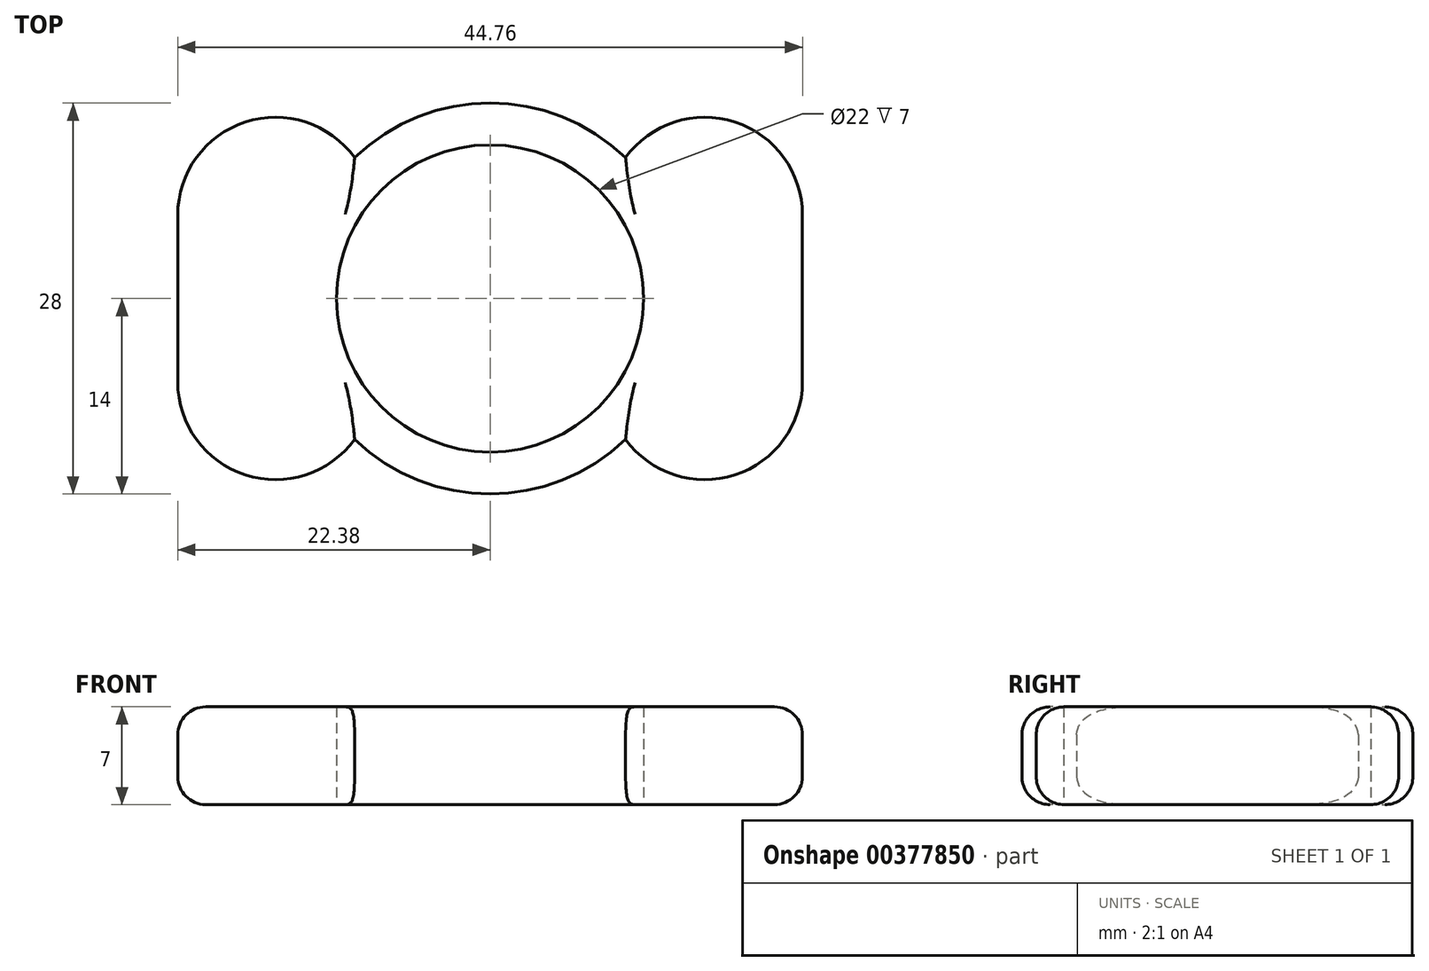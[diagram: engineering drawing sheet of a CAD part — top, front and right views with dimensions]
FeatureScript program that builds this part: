
annotation { "Feature Type Name" : "Feature", "Feature Type Description" : "" }
export const myFeature = defineFeature(function(context is Context, id is Id, definition is map)
    precondition{}
    {
        {
            var Q0;
            Q0=qCreatedBy(makeId("Top.planeOp"),FACE);
            var sketch = newSketch(context, id + "F0", { "sketchPlane" : qUnion([Q0])});
            skCircle(sketch, "E0", {"center": v(0, 0) * mm, "radius": 11 * mm});
            skCircle(sketch, "E1", {"center": v(15.38, -5.98) * mm, "radius": 5.25 * mm});
            skCircle(sketch, "E2", {"center": v(15.38, 5.98) * mm, "radius": 5.25 * mm});
            skCircle(sketch, "E3", {"center": v(-15.38, -5.98) * mm, "radius": 5.25 * mm});
            skCircle(sketch, "E4", {"center": v(-15.38, 5.98) * mm, "radius": 5.25 * mm});
            skCircle(sketch, "E5", {"center": v(0, 0) * mm, "radius": 14 * mm});
            skCircle(sketch, "E6", {"center": v(-15.38, 5.98) * mm, "radius": 7 * mm});
            skCircle(sketch, "E7", {"center": v(-15.38, -5.98) * mm, "radius": 7 * mm});
            skCircle(sketch, "E8", {"center": v(15.38, 5.98) * mm, "radius": 7 * mm});
            skCircle(sketch, "E9", {"center": v(15.38, -5.98) * mm, "radius": 7 * mm});
            skLineSegment(sketch, "E10", {"start": v(-22.38, 5.98) * mm, "end": v(-22.38, -5.98) * mm});
            skLineSegment(sketch, "E11", {"start": v(22.38, 5.98) * mm, "end": v(22.38, -5.98) * mm});
            skLineSegment(sketch, "E12", {"start": v(8.85, -3.44) * mm, "end": v(10.25, -3.99) * mm});
            skLineSegment(sketch, "E13", {"start": v(8.85, 3.44) * mm, "end": v(10.25, 3.99) * mm});
            skLineSegment(sketch, "E14", {"start": v(-8.85, -3.44) * mm, "end": v(-10.25, -3.99) * mm});
            skLineSegment(sketch, "E15", {"start": v(-10.25, -3.99) * mm, "end": v(-8.85, -3.44) * mm});
            skLineSegment(sketch, "E16", {"start": v(-8.85, 3.44) * mm, "end": v(-10.25, 3.99) * mm});
            skSolve(sketch);
        }
        {
            var Q0;
            {var subQ5=sQuery(id+"F0.wireOp",EDGE,"E7");var subQ8=sQuery(id+"F0.wireOp",EDGE,"E0");var subQ10=makeQuery(id+"F0.imprint","INTERSECT",VERTEX,{"disambiguationData":[OD(0.0)],"derivedFrom":[subQ8,subQ5]});Q0=makeQuery(id+"F0.imprint","IMPRINT",FACE,{"disambiguationData":[TD([[makeQuery(id+"F0.imprint","IMPRINT",EDGE,{"disambiguationData":[TD([[subQ10,-1.0]])],"derivedFrom":subQ8}),-1.0]])]});}
            var Q1;
            {var subQ0=sQuery(id+"F0.wireOp",EDGE,"E6");var subQ1=sQuery(id+"F0.wireOp",EDGE,"E3");var subQ11=makeQuery(id+"F0.imprint","INTERSECT",VERTEX,{"disambiguationData":[OD(0.0)],"derivedFrom":[subQ1,subQ0]});Q1=makeQuery(id+"F0.imprint","IMPRINT",FACE,{"disambiguationData":[TD([[makeQuery(id+"F0.imprint","IMPRINT",EDGE,{"disambiguationData":[TD([[subQ11,-1.0]])],"derivedFrom":subQ1}),-1.0]])]});}
            var Q2;
            {var subQ2=sQuery(id+"F0.wireOp",EDGE,"E6");var subQ4=sQuery(id+"F0.wireOp",EDGE,"E3");var subQ5=makeQuery(id+"F0.imprint","INTERSECT",VERTEX,{"disambiguationData":[OD(1.0)],"derivedFrom":[subQ4,subQ2]});Q2=makeQuery(id+"F0.imprint","IMPRINT",FACE,{"disambiguationData":[TD([[makeQuery(id+"F0.imprint","IMPRINT",EDGE,{"disambiguationData":[TD([[subQ5,-1.0]])],"derivedFrom":subQ4}),-1.0]])]});}
            var Q3;
            {var subQ0=sQuery(id+"F0.wireOp",EDGE,"E7");var subQ1=sQuery(id+"F0.wireOp",EDGE,"E5");var subQ2=makeQuery(id+"F0.imprint","INTERSECT",VERTEX,{"disambiguationData":[OD(1.0)],"derivedFrom":[subQ1,subQ0]});Q3=makeQuery(id+"F0.imprint","IMPRINT",FACE,{"disambiguationData":[TD([[makeQuery(id+"F0.imprint","IMPRINT",EDGE,{"disambiguationData":[TD([[subQ2,-1.0]])],"derivedFrom":subQ1}),1.0]])]});}
            var Q4;
            {var subQ0=sQuery(id+"F0.wireOp",EDGE,"E6");var subQ1=sQuery(id+"F0.wireOp",EDGE,"E3");var subQ2=makeQuery(id+"F0.imprint","INTERSECT",VERTEX,{"disambiguationData":[OD(0.0)],"derivedFrom":[subQ1,subQ0]});Q4=makeQuery(id+"F0.imprint","IMPRINT",FACE,{"disambiguationData":[TD([[makeQuery(id+"F0.imprint","IMPRINT",EDGE,{"disambiguationData":[TD([[subQ2,1.0]])],"derivedFrom":subQ1}),-1.0]])]});}
            var Q5;
            {var subQ0=sQuery(id+"F0.wireOp",EDGE,"E7");var subQ1=sQuery(id+"F0.wireOp",EDGE,"E4");var subQ2=makeQuery(id+"F0.imprint","INTERSECT",VERTEX,{"disambiguationData":[OD(1.0)],"derivedFrom":[subQ1,subQ0]});Q5=makeQuery(id+"F0.imprint","IMPRINT",FACE,{"disambiguationData":[TD([[makeQuery(id+"F0.imprint","IMPRINT",EDGE,{"disambiguationData":[TD([[subQ2,-1.0]])],"derivedFrom":subQ1}),-1.0]])]});}
            var Q6;
            {var subQ0=sQuery(id+"F0.wireOp",EDGE,"E6");var subQ1=sQuery(id+"F0.wireOp",EDGE,"E0");var subQ2=makeQuery(id+"F0.imprint","INTERSECT",VERTEX,{"disambiguationData":[OD(1.0)],"derivedFrom":[subQ1,subQ0]});Q6=makeQuery(id+"F0.imprint","IMPRINT",FACE,{"disambiguationData":[TD([[makeQuery(id+"F0.imprint","IMPRINT",EDGE,{"disambiguationData":[TD([[subQ2,-1.0]])],"derivedFrom":subQ1}),-1.0]])]});}
            var Q7;
            {var subQ5=sQuery(id+"F0.wireOp",EDGE,"E6");var subQ9=sQuery(id+"F0.wireOp",EDGE,"E0");var subQ10=makeQuery(id+"F0.imprint","INTERSECT",VERTEX,{"disambiguationData":[OD(0.0)],"derivedFrom":[subQ9,subQ5]});Q7=makeQuery(id+"F0.imprint","IMPRINT",FACE,{"disambiguationData":[TD([[makeQuery(id+"F0.imprint","IMPRINT",EDGE,{"disambiguationData":[TD([[subQ10,-1.0]])],"derivedFrom":subQ9}),-1.0]])]});}
            var Q8;
            {var subQ2=sQuery(id+"F0.wireOp",EDGE,"E7");var subQ4=sQuery(id+"F0.wireOp",EDGE,"E4");var subQ5=makeQuery(id+"F0.imprint","INTERSECT",VERTEX,{"disambiguationData":[OD(0.0)],"derivedFrom":[subQ4,subQ2]});Q8=makeQuery(id+"F0.imprint","IMPRINT",FACE,{"disambiguationData":[TD([[makeQuery(id+"F0.imprint","IMPRINT",EDGE,{"disambiguationData":[TD([[subQ5,1.0]])],"derivedFrom":subQ4}),-1.0]])]});}
            var Q9;
            {var subQ0=sQuery(id+"F0.wireOp",EDGE,"E8");var subQ1=sQuery(id+"F0.wireOp",EDGE,"E0");var subQ2=makeQuery(id+"F0.imprint","INTERSECT",VERTEX,{"disambiguationData":[OD(0.0)],"derivedFrom":[subQ1,subQ0]});Q9=makeQuery(id+"F0.imprint","IMPRINT",FACE,{"disambiguationData":[TD([[makeQuery(id+"F0.imprint","IMPRINT",EDGE,{"disambiguationData":[TD([[subQ2,-1.0]])],"derivedFrom":subQ1}),-1.0]])]});}
            var Q10;
            {var subQ0=sQuery(id+"F0.wireOp",EDGE,"E7");var subQ1=sQuery(id+"F0.wireOp",EDGE,"E0");var subQ2=makeQuery(id+"F0.imprint","INTERSECT",VERTEX,{"disambiguationData":[OD(1.0)],"derivedFrom":[subQ1,subQ0]});Q10=makeQuery(id+"F0.imprint","IMPRINT",FACE,{"disambiguationData":[TD([[makeQuery(id+"F0.imprint","IMPRINT",EDGE,{"disambiguationData":[TD([[subQ2,-1.0]])],"derivedFrom":subQ1}),-1.0]])]});}
            var Q11;
            {var subQ6=sQuery(id+"F0.wireOp",EDGE,"E9");var subQ8=sQuery(id+"F0.wireOp",EDGE,"E0");var subQ9=makeQuery(id+"F0.imprint","INTERSECT",VERTEX,{"disambiguationData":[OD(0.0)],"derivedFrom":[subQ8,subQ6]});Q11=makeQuery(id+"F0.imprint","IMPRINT",FACE,{"disambiguationData":[TD([[makeQuery(id+"F0.imprint","IMPRINT",EDGE,{"disambiguationData":[TD([[subQ9,-1.0]])],"derivedFrom":subQ8}),-1.0]])]});}
            var Q12;
            {var subQ0=sQuery(id+"F0.wireOp",EDGE,"E9");var subQ1=sQuery(id+"F0.wireOp",EDGE,"E5");var subQ2=makeQuery(id+"F0.imprint","INTERSECT",VERTEX,{"disambiguationData":[OD(1.0)],"derivedFrom":[subQ1,subQ0]});Q12=makeQuery(id+"F0.imprint","IMPRINT",FACE,{"disambiguationData":[TD([[makeQuery(id+"F0.imprint","IMPRINT",EDGE,{"disambiguationData":[TD([[subQ2,1.0]])],"derivedFrom":subQ1}),1.0]])]});}
            var Q13;
            {var subQ0=sQuery(id+"F0.wireOp",EDGE,"E8");var subQ5=sQuery(id+"F0.wireOp",EDGE,"E0");var subQ6=makeQuery(id+"F0.imprint","INTERSECT",VERTEX,{"disambiguationData":[OD(0.0)],"derivedFrom":[subQ5,subQ0]});Q13=makeQuery(id+"F0.imprint","IMPRINT",FACE,{"disambiguationData":[TD([[makeQuery(id+"F0.imprint","IMPRINT",EDGE,{"disambiguationData":[TD([[subQ6,1.0]])],"derivedFrom":subQ5}),-1.0]])]});}
            var Q14;
            {var subQ2=sQuery(id+"F0.wireOp",EDGE,"E5");var subQ6=sQuery(id+"F0.wireOp",EDGE,"E2");var subQ7=makeQuery(id+"F0.imprint","INTERSECT",VERTEX,{"disambiguationData":[OD(1.0)],"derivedFrom":[subQ6,subQ2]});Q14=makeQuery(id+"F0.imprint","IMPRINT",FACE,{"disambiguationData":[TD([[makeQuery(id+"F0.imprint","IMPRINT",EDGE,{"disambiguationData":[TD([[subQ7,1.0]])],"derivedFrom":subQ6}),-1.0]])]});}
            var Q15;
            {var subQ0=sQuery(id+"F0.wireOp",EDGE,"E11");Q15=makeQuery(id+"F0.imprint","IMPRINT",FACE,{"disambiguationData":[TD([[makeQuery(id+"F0.imprint","IMPRINT",EDGE,{"derivedFrom":subQ0}),-1.0]])]});}
            var Q16;
            {var subQ2=sQuery(id+"F0.wireOp",EDGE,"E8");var subQ4=sQuery(id+"F0.wireOp",EDGE,"E1");var subQ5=makeQuery(id+"F0.imprint","INTERSECT",VERTEX,{"disambiguationData":[OD(1.0)],"derivedFrom":[subQ4,subQ2]});Q16=makeQuery(id+"F0.imprint","IMPRINT",FACE,{"disambiguationData":[TD([[makeQuery(id+"F0.imprint","IMPRINT",EDGE,{"disambiguationData":[TD([[subQ5,1.0]])],"derivedFrom":subQ4}),-1.0]])]});}
            var Q17;
            {var subQ3=sQuery(id+"F0.wireOp",EDGE,"E8");var subQ8=sQuery(id+"F0.wireOp",EDGE,"E1");var subQ9=makeQuery(id+"F0.imprint","INTERSECT",VERTEX,{"disambiguationData":[OD(0.0)],"derivedFrom":[subQ8,subQ3]});Q17=makeQuery(id+"F0.imprint","IMPRINT",FACE,{"disambiguationData":[TD([[makeQuery(id+"F0.imprint","IMPRINT",EDGE,{"disambiguationData":[TD([[subQ9,1.0]])],"derivedFrom":subQ8}),-1.0]])]});}
            var Q18;
            {var subQ0=sQuery(id+"F0.wireOp",EDGE,"E8");var subQ1=sQuery(id+"F0.wireOp",EDGE,"E0");var subQ2=makeQuery(id+"F0.imprint","INTERSECT",VERTEX,{"disambiguationData":[OD(1.0)],"derivedFrom":[subQ1,subQ0]});Q18=makeQuery(id+"F0.imprint","IMPRINT",FACE,{"disambiguationData":[TD([[makeQuery(id+"F0.imprint","IMPRINT",EDGE,{"disambiguationData":[TD([[subQ2,1.0]])],"derivedFrom":subQ1}),-1.0]])]});}
            var Q19;
            {var subQ0=sQuery(id+"F0.wireOp",EDGE,"E8");var subQ1=sQuery(id+"F0.wireOp",EDGE,"E1");var subQ2=makeQuery(id+"F0.imprint","INTERSECT",VERTEX,{"disambiguationData":[OD(0.0)],"derivedFrom":[subQ1,subQ0]});Q19=makeQuery(id+"F0.imprint","IMPRINT",FACE,{"disambiguationData":[TD([[makeQuery(id+"F0.imprint","IMPRINT",EDGE,{"disambiguationData":[TD([[subQ2,-1.0]])],"derivedFrom":subQ1}),-1.0]])]});}
            var Q20;
            {var subQ0=sQuery(id+"F0.wireOp",EDGE,"E5");var subQ1=sQuery(id+"F0.wireOp",EDGE,"E2");var subQ2=makeQuery(id+"F0.imprint","INTERSECT",VERTEX,{"disambiguationData":[OD(0.0)],"derivedFrom":[subQ1,subQ0]});Q20=makeQuery(id+"F0.imprint","IMPRINT",FACE,{"disambiguationData":[TD([[makeQuery(id+"F0.imprint","IMPRINT",EDGE,{"disambiguationData":[TD([[subQ2,-1.0]])],"derivedFrom":subQ1}),-1.0]])]});}
            var Q21;
            {var subQ0=sQuery(id+"F0.wireOp",EDGE,"E10");Q21=makeQuery(id+"F0.imprint","IMPRINT",FACE,{"disambiguationData":[TD([[makeQuery(id+"F0.imprint","IMPRINT",EDGE,{"derivedFrom":subQ0}),1.0]])]});}
            var Q22;
            {var subQ0=sQuery(id+"F0.wireOp",EDGE,"E8");var subQ1=sQuery(id+"F0.wireOp",EDGE,"E0");var subQ2=makeQuery(id+"F0.imprint","INTERSECT",VERTEX,{"disambiguationData":[OD(1.0)],"derivedFrom":[subQ1,subQ0]});Q22=makeQuery(id+"F0.imprint","IMPRINT",FACE,{"disambiguationData":[TD([[makeQuery(id+"F0.imprint","IMPRINT",EDGE,{"disambiguationData":[TD([[subQ2,-1.0]])],"derivedFrom":subQ1}),-1.0]])]});}
            extrude(context, id + "F1", {"entities" : qUnion([Q0, Q1, Q2, Q3, Q4, Q5, Q6, Q7, Q8, Q9, Q10, Q11, Q12, Q13, Q14, Q15, Q16, Q17, Q18, Q19, Q20, Q21, Q22]), "depth" : 7 * mm});
        }
        {
            var Q0;
            {var subQ5=sQuery(id+"F0.wireOp",EDGE,"E7");var subQ8=sQuery(id+"F0.wireOp",EDGE,"E0");var subQ10=makeQuery(id+"F0.imprint","INTERSECT",VERTEX,{"disambiguationData":[OD(0.0)],"derivedFrom":[subQ8,subQ5]});Q0=makeQuery(id+"F0.imprint","IMPRINT",FACE,{"disambiguationData":[TD([[makeQuery(id+"F0.imprint","IMPRINT",EDGE,{"disambiguationData":[TD([[subQ10,-1.0]])],"derivedFrom":subQ8}),-1.0]])]});}
            var Q1;
            {var subQ2=sQuery(id+"F0.wireOp",EDGE,"E6");var subQ4=sQuery(id+"F0.wireOp",EDGE,"E3");var subQ5=makeQuery(id+"F0.imprint","INTERSECT",VERTEX,{"disambiguationData":[OD(1.0)],"derivedFrom":[subQ4,subQ2]});Q1=makeQuery(id+"F0.imprint","IMPRINT",FACE,{"disambiguationData":[TD([[makeQuery(id+"F0.imprint","IMPRINT",EDGE,{"disambiguationData":[TD([[subQ5,-1.0]])],"derivedFrom":subQ4}),-1.0]])]});}
            var Q2;
            {var subQ0=sQuery(id+"F0.wireOp",EDGE,"E6");var subQ1=sQuery(id+"F0.wireOp",EDGE,"E3");var subQ11=makeQuery(id+"F0.imprint","INTERSECT",VERTEX,{"disambiguationData":[OD(0.0)],"derivedFrom":[subQ1,subQ0]});Q2=makeQuery(id+"F0.imprint","IMPRINT",FACE,{"disambiguationData":[TD([[makeQuery(id+"F0.imprint","IMPRINT",EDGE,{"disambiguationData":[TD([[subQ11,-1.0]])],"derivedFrom":subQ1}),-1.0]])]});}
            var Q3;
            {var subQ2=sQuery(id+"F0.wireOp",EDGE,"E7");var subQ4=sQuery(id+"F0.wireOp",EDGE,"E4");var subQ5=makeQuery(id+"F0.imprint","INTERSECT",VERTEX,{"disambiguationData":[OD(0.0)],"derivedFrom":[subQ4,subQ2]});Q3=makeQuery(id+"F0.imprint","IMPRINT",FACE,{"disambiguationData":[TD([[makeQuery(id+"F0.imprint","IMPRINT",EDGE,{"disambiguationData":[TD([[subQ5,1.0]])],"derivedFrom":subQ4}),-1.0]])]});}
            var Q4;
            {var subQ0=sQuery(id+"F0.wireOp",EDGE,"E8");var subQ1=sQuery(id+"F0.wireOp",EDGE,"E0");var subQ2=makeQuery(id+"F0.imprint","INTERSECT",VERTEX,{"disambiguationData":[OD(0.0)],"derivedFrom":[subQ1,subQ0]});Q4=makeQuery(id+"F0.imprint","IMPRINT",FACE,{"disambiguationData":[TD([[makeQuery(id+"F0.imprint","IMPRINT",EDGE,{"disambiguationData":[TD([[subQ2,-1.0]])],"derivedFrom":subQ1}),-1.0]])]});}
            var Q5;
            {var subQ0=sQuery(id+"F0.wireOp",EDGE,"E5");var subQ1=sQuery(id+"F0.wireOp",EDGE,"E4");var subQ2=makeQuery(id+"F0.imprint","INTERSECT",VERTEX,{"disambiguationData":[OD(0.0)],"derivedFrom":[subQ1,subQ0]});Q5=makeQuery(id+"F0.imprint","IMPRINT",FACE,{"disambiguationData":[TD([[makeQuery(id+"F0.imprint","IMPRINT",EDGE,{"disambiguationData":[TD([[subQ2,1.0]])],"derivedFrom":subQ1}),1.0]])]});}
            var Q6;
            {var subQ0=sQuery(id+"F0.wireOp",EDGE,"E7");var subQ1=sQuery(id+"F0.wireOp",EDGE,"E4");var subQ2=makeQuery(id+"F0.imprint","INTERSECT",VERTEX,{"disambiguationData":[OD(0.0)],"derivedFrom":[subQ1,subQ0]});Q6=makeQuery(id+"F0.imprint","IMPRINT",FACE,{"disambiguationData":[TD([[makeQuery(id+"F0.imprint","IMPRINT",EDGE,{"disambiguationData":[TD([[subQ2,1.0]])],"derivedFrom":subQ1}),1.0]])]});}
            var Q7;
            {var subQ5=sQuery(id+"F0.wireOp",EDGE,"E6");var subQ9=sQuery(id+"F0.wireOp",EDGE,"E0");var subQ10=makeQuery(id+"F0.imprint","INTERSECT",VERTEX,{"disambiguationData":[OD(0.0)],"derivedFrom":[subQ9,subQ5]});Q7=makeQuery(id+"F0.imprint","IMPRINT",FACE,{"disambiguationData":[TD([[makeQuery(id+"F0.imprint","IMPRINT",EDGE,{"disambiguationData":[TD([[subQ10,-1.0]])],"derivedFrom":subQ9}),-1.0]])]});}
            var Q8;
            {var subQ0=sQuery(id+"F0.wireOp",EDGE,"E7");var subQ1=sQuery(id+"F0.wireOp",EDGE,"E5");var subQ2=makeQuery(id+"F0.imprint","INTERSECT",VERTEX,{"disambiguationData":[OD(1.0)],"derivedFrom":[subQ1,subQ0]});Q8=makeQuery(id+"F0.imprint","IMPRINT",FACE,{"disambiguationData":[TD([[makeQuery(id+"F0.imprint","IMPRINT",EDGE,{"disambiguationData":[TD([[subQ2,-1.0]])],"derivedFrom":subQ1}),1.0]])]});}
            var Q9;
            {var subQ0=sQuery(id+"F0.wireOp",EDGE,"E5");var subQ1=sQuery(id+"F0.wireOp",EDGE,"E3");var subQ2=makeQuery(id+"F0.imprint","INTERSECT",VERTEX,{"disambiguationData":[OD(0.0)],"derivedFrom":[subQ1,subQ0]});Q9=makeQuery(id+"F0.imprint","IMPRINT",FACE,{"disambiguationData":[TD([[makeQuery(id+"F0.imprint","IMPRINT",EDGE,{"disambiguationData":[TD([[subQ2,1.0]])],"derivedFrom":subQ1}),1.0]])]});}
            var Q10;
            {var subQ0=sQuery(id+"F0.wireOp",EDGE,"E7");var subQ1=sQuery(id+"F0.wireOp",EDGE,"E0");var subQ2=makeQuery(id+"F0.imprint","INTERSECT",VERTEX,{"disambiguationData":[OD(1.0)],"derivedFrom":[subQ1,subQ0]});Q10=makeQuery(id+"F0.imprint","IMPRINT",FACE,{"disambiguationData":[TD([[makeQuery(id+"F0.imprint","IMPRINT",EDGE,{"disambiguationData":[TD([[subQ2,-1.0]])],"derivedFrom":subQ1}),-1.0]])]});}
            var Q11;
            {var subQ6=sQuery(id+"F0.wireOp",EDGE,"E9");var subQ8=sQuery(id+"F0.wireOp",EDGE,"E0");var subQ9=makeQuery(id+"F0.imprint","INTERSECT",VERTEX,{"disambiguationData":[OD(0.0)],"derivedFrom":[subQ8,subQ6]});Q11=makeQuery(id+"F0.imprint","IMPRINT",FACE,{"disambiguationData":[TD([[makeQuery(id+"F0.imprint","IMPRINT",EDGE,{"disambiguationData":[TD([[subQ9,-1.0]])],"derivedFrom":subQ8}),-1.0]])]});}
            var Q12;
            {var subQ0=sQuery(id+"F0.wireOp",EDGE,"E6");var subQ1=sQuery(id+"F0.wireOp",EDGE,"E3");var subQ2=makeQuery(id+"F0.imprint","INTERSECT",VERTEX,{"disambiguationData":[OD(0.0)],"derivedFrom":[subQ1,subQ0]});Q12=makeQuery(id+"F0.imprint","IMPRINT",FACE,{"disambiguationData":[TD([[makeQuery(id+"F0.imprint","IMPRINT",EDGE,{"disambiguationData":[TD([[subQ2,1.0]])],"derivedFrom":subQ1}),1.0]])]});}
            var Q13;
            {var subQ0=sQuery(id+"F0.wireOp",EDGE,"E5");var subQ1=sQuery(id+"F0.wireOp",EDGE,"E1");var subQ2=makeQuery(id+"F0.imprint","INTERSECT",VERTEX,{"disambiguationData":[OD(0.0)],"derivedFrom":[subQ1,subQ0]});Q13=makeQuery(id+"F0.imprint","IMPRINT",FACE,{"disambiguationData":[TD([[makeQuery(id+"F0.imprint","IMPRINT",EDGE,{"disambiguationData":[TD([[subQ2,-1.0]])],"derivedFrom":subQ1}),1.0]])]});}
            var Q14;
            {var subQ0=sQuery(id+"F0.wireOp",EDGE,"E9");var subQ1=sQuery(id+"F0.wireOp",EDGE,"E5");var subQ2=makeQuery(id+"F0.imprint","INTERSECT",VERTEX,{"disambiguationData":[OD(1.0)],"derivedFrom":[subQ1,subQ0]});Q14=makeQuery(id+"F0.imprint","IMPRINT",FACE,{"disambiguationData":[TD([[makeQuery(id+"F0.imprint","IMPRINT",EDGE,{"disambiguationData":[TD([[subQ2,1.0]])],"derivedFrom":subQ1}),1.0]])]});}
            var Q15;
            {var subQ0=sQuery(id+"F0.wireOp",EDGE,"E8");var subQ5=sQuery(id+"F0.wireOp",EDGE,"E0");var subQ6=makeQuery(id+"F0.imprint","INTERSECT",VERTEX,{"disambiguationData":[OD(0.0)],"derivedFrom":[subQ5,subQ0]});Q15=makeQuery(id+"F0.imprint","IMPRINT",FACE,{"disambiguationData":[TD([[makeQuery(id+"F0.imprint","IMPRINT",EDGE,{"disambiguationData":[TD([[subQ6,1.0]])],"derivedFrom":subQ5}),-1.0]])]});}
            var Q16;
            {var subQ0=sQuery(id+"F0.wireOp",EDGE,"E5");var subQ1=sQuery(id+"F0.wireOp",EDGE,"E2");var subQ2=makeQuery(id+"F0.imprint","INTERSECT",VERTEX,{"disambiguationData":[OD(0.0)],"derivedFrom":[subQ1,subQ0]});Q16=makeQuery(id+"F0.imprint","IMPRINT",FACE,{"disambiguationData":[TD([[makeQuery(id+"F0.imprint","IMPRINT",EDGE,{"disambiguationData":[TD([[subQ2,1.0]])],"derivedFrom":subQ1}),1.0]])]});}
            var Q17;
            {var subQ2=sQuery(id+"F0.wireOp",EDGE,"E5");var subQ6=sQuery(id+"F0.wireOp",EDGE,"E2");var subQ7=makeQuery(id+"F0.imprint","INTERSECT",VERTEX,{"disambiguationData":[OD(1.0)],"derivedFrom":[subQ6,subQ2]});Q17=makeQuery(id+"F0.imprint","IMPRINT",FACE,{"disambiguationData":[TD([[makeQuery(id+"F0.imprint","IMPRINT",EDGE,{"disambiguationData":[TD([[subQ7,1.0]])],"derivedFrom":subQ6}),-1.0]])]});}
            var Q18;
            {var subQ3=sQuery(id+"F0.wireOp",EDGE,"E8");var subQ8=sQuery(id+"F0.wireOp",EDGE,"E1");var subQ9=makeQuery(id+"F0.imprint","INTERSECT",VERTEX,{"disambiguationData":[OD(0.0)],"derivedFrom":[subQ8,subQ3]});Q18=makeQuery(id+"F0.imprint","IMPRINT",FACE,{"disambiguationData":[TD([[makeQuery(id+"F0.imprint","IMPRINT",EDGE,{"disambiguationData":[TD([[subQ9,1.0]])],"derivedFrom":subQ8}),-1.0]])]});}
            var Q19;
            {var subQ0=sQuery(id+"F0.wireOp",EDGE,"E6");var subQ1=sQuery(id+"F0.wireOp",EDGE,"E3");var subQ2=makeQuery(id+"F0.imprint","INTERSECT",VERTEX,{"disambiguationData":[OD(0.0)],"derivedFrom":[subQ1,subQ0]});Q19=makeQuery(id+"F0.imprint","IMPRINT",FACE,{"disambiguationData":[TD([[makeQuery(id+"F0.imprint","IMPRINT",EDGE,{"disambiguationData":[TD([[subQ2,1.0]])],"derivedFrom":subQ1}),-1.0]])]});}
            var Q20;
            {var subQ0=sQuery(id+"F0.wireOp",EDGE,"E7");var subQ1=sQuery(id+"F0.wireOp",EDGE,"E4");var subQ2=makeQuery(id+"F0.imprint","INTERSECT",VERTEX,{"disambiguationData":[OD(1.0)],"derivedFrom":[subQ1,subQ0]});Q20=makeQuery(id+"F0.imprint","IMPRINT",FACE,{"disambiguationData":[TD([[makeQuery(id+"F0.imprint","IMPRINT",EDGE,{"disambiguationData":[TD([[subQ2,-1.0]])],"derivedFrom":subQ1}),-1.0]])]});}
            var Q21;
            {var subQ2=sQuery(id+"F0.wireOp",EDGE,"E8");var subQ4=sQuery(id+"F0.wireOp",EDGE,"E1");var subQ5=makeQuery(id+"F0.imprint","INTERSECT",VERTEX,{"disambiguationData":[OD(1.0)],"derivedFrom":[subQ4,subQ2]});Q21=makeQuery(id+"F0.imprint","IMPRINT",FACE,{"disambiguationData":[TD([[makeQuery(id+"F0.imprint","IMPRINT",EDGE,{"disambiguationData":[TD([[subQ5,1.0]])],"derivedFrom":subQ4}),-1.0]])]});}
            var Q22;
            {var subQ0=sQuery(id+"F0.wireOp",EDGE,"E8");var subQ1=sQuery(id+"F0.wireOp",EDGE,"E1");var subQ2=makeQuery(id+"F0.imprint","INTERSECT",VERTEX,{"disambiguationData":[OD(0.0)],"derivedFrom":[subQ1,subQ0]});Q22=makeQuery(id+"F0.imprint","IMPRINT",FACE,{"disambiguationData":[TD([[makeQuery(id+"F0.imprint","IMPRINT",EDGE,{"disambiguationData":[TD([[subQ2,-1.0]])],"derivedFrom":subQ1}),1.0]])]});}
            var Q23;
            {var subQ0=sQuery(id+"F0.wireOp",EDGE,"E7");var subQ1=sQuery(id+"F0.wireOp",EDGE,"E4");var subQ2=makeQuery(id+"F0.imprint","INTERSECT",VERTEX,{"disambiguationData":[OD(0.0)],"derivedFrom":[subQ1,subQ0]});Q23=makeQuery(id+"F0.imprint","IMPRINT",FACE,{"disambiguationData":[TD([[makeQuery(id+"F0.imprint","IMPRINT",EDGE,{"disambiguationData":[TD([[subQ2,-1.0]])],"derivedFrom":subQ1}),1.0]])]});}
            var Q24;
            {var subQ0=sQuery(id+"F0.wireOp",EDGE,"E6");var subQ1=sQuery(id+"F0.wireOp",EDGE,"E3");var subQ2=makeQuery(id+"F0.imprint","INTERSECT",VERTEX,{"disambiguationData":[OD(0.0)],"derivedFrom":[subQ1,subQ0]});Q24=makeQuery(id+"F0.imprint","IMPRINT",FACE,{"disambiguationData":[TD([[makeQuery(id+"F0.imprint","IMPRINT",EDGE,{"disambiguationData":[TD([[subQ2,-1.0]])],"derivedFrom":subQ1}),1.0]])]});}
            var Q25;
            {var subQ0=sQuery(id+"F0.wireOp",EDGE,"E8");var subQ1=sQuery(id+"F0.wireOp",EDGE,"E1");var subQ2=makeQuery(id+"F0.imprint","INTERSECT",VERTEX,{"disambiguationData":[OD(0.0)],"derivedFrom":[subQ1,subQ0]});Q25=makeQuery(id+"F0.imprint","IMPRINT",FACE,{"disambiguationData":[TD([[makeQuery(id+"F0.imprint","IMPRINT",EDGE,{"disambiguationData":[TD([[subQ2,-1.0]])],"derivedFrom":subQ1}),-1.0]])]});}
            var Q26;
            {var subQ0=sQuery(id+"F0.wireOp",EDGE,"E8");var subQ1=sQuery(id+"F0.wireOp",EDGE,"E1");var subQ2=makeQuery(id+"F0.imprint","INTERSECT",VERTEX,{"disambiguationData":[OD(0.0)],"derivedFrom":[subQ1,subQ0]});Q26=makeQuery(id+"F0.imprint","IMPRINT",FACE,{"disambiguationData":[TD([[makeQuery(id+"F0.imprint","IMPRINT",EDGE,{"disambiguationData":[TD([[subQ2,1.0]])],"derivedFrom":subQ1}),1.0]])]});}
            var Q27;
            {var subQ0=sQuery(id+"F0.wireOp",EDGE,"E5");var subQ1=sQuery(id+"F0.wireOp",EDGE,"E2");var subQ2=makeQuery(id+"F0.imprint","INTERSECT",VERTEX,{"disambiguationData":[OD(0.0)],"derivedFrom":[subQ1,subQ0]});Q27=makeQuery(id+"F0.imprint","IMPRINT",FACE,{"disambiguationData":[TD([[makeQuery(id+"F0.imprint","IMPRINT",EDGE,{"disambiguationData":[TD([[subQ2,-1.0]])],"derivedFrom":subQ1}),-1.0]])]});}
            var Q28;
            {var subQ0=sQuery(id+"F0.wireOp",EDGE,"E9");var subQ1=sQuery(id+"F0.wireOp",EDGE,"E2");var subQ2=makeQuery(id+"F0.imprint","INTERSECT",VERTEX,{"disambiguationData":[OD(0.0)],"derivedFrom":[subQ1,subQ0]});Q28=makeQuery(id+"F0.imprint","IMPRINT",FACE,{"disambiguationData":[TD([[makeQuery(id+"F0.imprint","IMPRINT",EDGE,{"disambiguationData":[TD([[subQ2,-1.0]])],"derivedFrom":subQ1}),1.0]])]});}
            var Q29;
            {var subQ0=sQuery(id+"F0.wireOp",EDGE,"E8");var subQ1=sQuery(id+"F0.wireOp",EDGE,"E0");var subQ2=makeQuery(id+"F0.imprint","INTERSECT",VERTEX,{"disambiguationData":[OD(1.0)],"derivedFrom":[subQ1,subQ0]});Q29=makeQuery(id+"F0.imprint","IMPRINT",FACE,{"disambiguationData":[TD([[makeQuery(id+"F0.imprint","IMPRINT",EDGE,{"disambiguationData":[TD([[subQ2,1.0]])],"derivedFrom":subQ1}),-1.0]])]});}
            var Q30;
            {var subQ0=sQuery(id+"F0.wireOp",EDGE,"E6");var subQ1=sQuery(id+"F0.wireOp",EDGE,"E0");var subQ2=makeQuery(id+"F0.imprint","INTERSECT",VERTEX,{"disambiguationData":[OD(1.0)],"derivedFrom":[subQ1,subQ0]});Q30=makeQuery(id+"F0.imprint","IMPRINT",FACE,{"disambiguationData":[TD([[makeQuery(id+"F0.imprint","IMPRINT",EDGE,{"disambiguationData":[TD([[subQ2,-1.0]])],"derivedFrom":subQ1}),-1.0]])]});}
            var Q31;
            {var subQ0=sQuery(id+"F0.wireOp",EDGE,"E5");var subQ1=sQuery(id+"F0.wireOp",EDGE,"E2");var subQ2=makeQuery(id+"F0.imprint","INTERSECT",VERTEX,{"disambiguationData":[OD(0.0)],"derivedFrom":[subQ1,subQ0]});Q31=makeQuery(id+"F0.imprint","IMPRINT",FACE,{"disambiguationData":[TD([[makeQuery(id+"F0.imprint","IMPRINT",EDGE,{"disambiguationData":[TD([[subQ2,-1.0]])],"derivedFrom":subQ1}),1.0]])]});}
            var Q32;
            {var subQ0=sQuery(id+"F0.wireOp",EDGE,"E11");Q32=makeQuery(id+"F0.imprint","IMPRINT",FACE,{"disambiguationData":[TD([[makeQuery(id+"F0.imprint","IMPRINT",EDGE,{"derivedFrom":subQ0}),-1.0]])]});}
            var Q33;
            {var subQ0=sQuery(id+"F0.wireOp",EDGE,"E10");Q33=makeQuery(id+"F0.imprint","IMPRINT",FACE,{"disambiguationData":[TD([[makeQuery(id+"F0.imprint","IMPRINT",EDGE,{"derivedFrom":subQ0}),1.0]])]});}
            extrude(context, id + "F2", {"entities" : qUnion([Q0, Q1, Q2, Q3, Q4, Q5, Q6, Q7, Q8, Q9, Q10, Q11, Q12, Q13, Q14, Q15, Q16, Q17, Q18, Q19, Q20, Q21, Q22, Q23, Q24, Q25, Q26, Q27, Q28, Q29, Q30, Q31, Q32, Q33]), "operationType" : NewBodyOperationType.ADD, "depth" : 7 * mm});
        }
        {
            var Q0;
            {var subQ0=sQuery(id+"F0.wireOp",EDGE,"E5");Q0=makeQuery(id+"F1.opExtrude","CAP_EDGE",EDGE,{"disambiguationData":[OSD([subQ0]),TDD([makeQuery(id+"F0.imprint","IMPRINT",EDGE,{"disambiguationData":[TD([[makeQuery(id+"F0.imprint","INTERSECT",VERTEX,{"disambiguationData":[OD(0.0)],"derivedFrom":[subQ0,sQuery(id+"F0.wireOp",EDGE,"E7")]}),-1.0]])],"derivedFrom":subQ0})])],"isStart":false});}
            var Q1;
            {var subQ0=sQuery(id+"F0.wireOp",EDGE,"E5");Q1=makeQuery(id+"F1.opExtrude","CAP_EDGE",EDGE,{"disambiguationData":[OSD([subQ0]),TDD([makeQuery(id+"F0.imprint","IMPRINT",EDGE,{"disambiguationData":[TD([[makeQuery(id+"F0.imprint","INTERSECT",VERTEX,{"disambiguationData":[OD(0.0)],"derivedFrom":[subQ0,sQuery(id+"F0.wireOp",EDGE,"E7")]}),-1.0]])],"derivedFrom":subQ0})])],"isStart":true});}
            var Q2;
            Q2=makeQuery(id+"F1.opExtrude","CAP_EDGE",EDGE,{"disambiguationData":[OSD([sQuery(id+"F0.wireOp",EDGE,"E9")])],"isStart":true});
            var Q3;
            {var subQ0=sQuery(id+"F0.wireOp",EDGE,"E5");Q3=makeQuery(id+"F1.opExtrude","CAP_EDGE",EDGE,{"disambiguationData":[OSD([subQ0]),TDD([makeQuery(id+"F0.imprint","IMPRINT",EDGE,{"disambiguationData":[TD([[makeQuery(id+"F0.imprint","INTERSECT",VERTEX,{"disambiguationData":[OD(0.0)],"derivedFrom":[subQ0,sQuery(id+"F0.wireOp",EDGE,"E8")]}),-1.0]])],"derivedFrom":subQ0})])],"isStart":true});}
            var Q4;
            Q4=makeQuery(id+"F1.opExtrude","CAP_EDGE",EDGE,{"disambiguationData":[OSD([sQuery(id+"F0.wireOp",EDGE,"E6")])],"isStart":true});
            var Q5;
            Q5=makeQuery(id+"F1.opExtrude","CAP_EDGE",EDGE,{"disambiguationData":[OSD([sQuery(id+"F0.wireOp",EDGE,"E7")])],"isStart":false});
            var Q6;
            {var subQ0=sQuery(id+"F0.wireOp",EDGE,"E5");Q6=makeQuery(id+"F1.opExtrude","CAP_EDGE",EDGE,{"disambiguationData":[OSD([subQ0]),TDD([makeQuery(id+"F0.imprint","IMPRINT",EDGE,{"disambiguationData":[TD([[makeQuery(id+"F0.imprint","INTERSECT",VERTEX,{"disambiguationData":[OD(0.0)],"derivedFrom":[subQ0,sQuery(id+"F0.wireOp",EDGE,"E8")]}),-1.0]])],"derivedFrom":subQ0})])],"isStart":false});}
            var Q7;
            Q7=makeQuery(id+"F1.opExtrude","CAP_EDGE",EDGE,{"disambiguationData":[OSD([sQuery(id+"F0.wireOp",EDGE,"E8")])],"isStart":false});
            fillet(context, id + "F3", {"entities" : qUnion([Q0, Q1, Q2, Q3, Q4, Q5, Q6, Q7]), "radius" : 2 * mm, "tangentPropagation" : true, "allowEdgeOverflow" : false});
        }
    });
